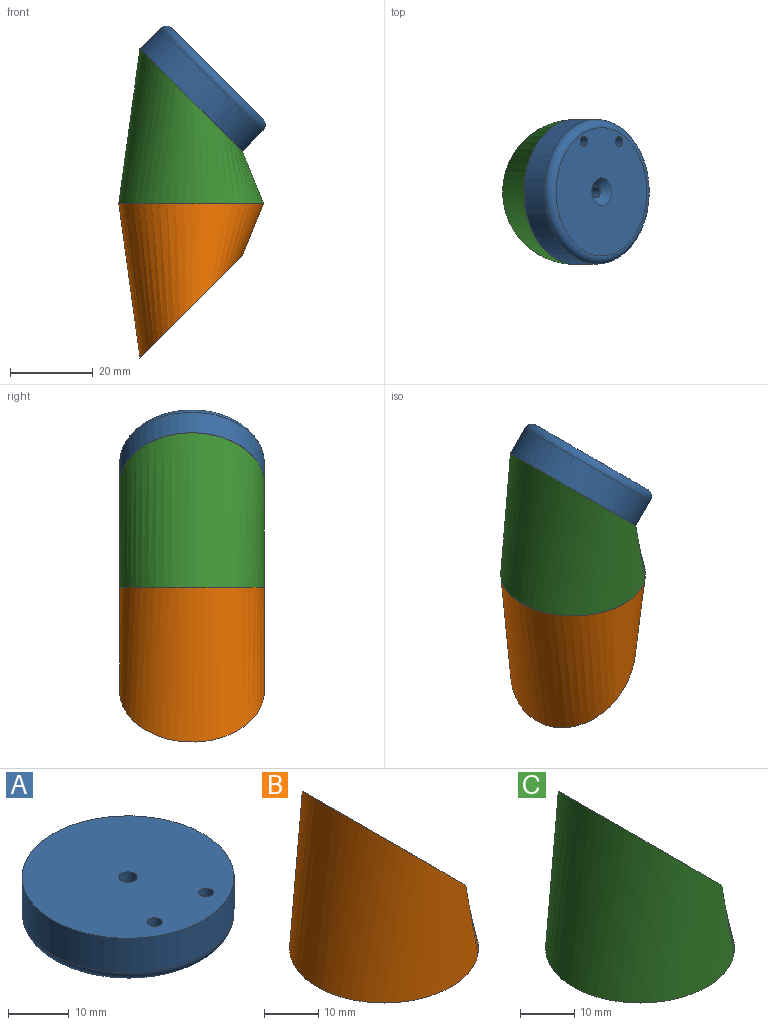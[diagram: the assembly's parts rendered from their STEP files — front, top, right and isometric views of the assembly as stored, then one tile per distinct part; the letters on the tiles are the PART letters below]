
ASSEMBLY  parts=3 mates=2
PART A: 8 faces, bbox 37.9x37.9x9 mm
  f0: cylinder r=17.5mm len=35mm, axis (0,0,-1), area 769.7mm2, adj f1,f7
  f1: plane 35x35mm, normal (0,0,1), area 945.2mm2, adj f0,f3,f5,f6
  f2: plane 31x31mm, normal (0,0,-1), area 709.5mm2, adj f4,f5,f6,f7
  f3: cylinder r=1.5mm len=7.14mm, axis (0,0,-1), area 67.3mm2, adj f1,f4
  f4: cone r=1.5mm half-angle=45deg, axis (0,0,-1), area 40.2mm2, adj f2,f3
  f5: cylinder r=1.25mm len=9mm, axis (0,0,-1), area 70.7mm2, adj f1,f2
  f6: cylinder r=1.25mm len=9mm, axis (0,0,-1), area 70.7mm2, adj f1,f2
  f7: torus R=15.5mm, axis (0,0,1), area 331.1mm2, adj f0,f2
PART B: 9 faces, bbox 35x35x37.4 mm
  f0: plane 35x35mm, normal (0,0,-1), area 956.3mm2, adj f2,f3
  f1: plane 35x24.75mm, normal (0.71,0,0.71), area 582mm2, adj f2,f5
  f2: bspline ~37.37x35mm, area 2581.6mm2, adj f0,f1
  f3: cylinder r=1.35mm len=12mm, axis (0,0,-1), area 101.8mm2, adj f0,f4
  f4: plane 2.7x2.7mm, normal (0,0,-1), area 5.7mm2, adj f3
  f5: cylinder r=11mm len=22mm, axis (0.71,0,0.71), area 449.2mm2, adj f1,f6
  f6: plane 22x15.56mm, normal (0.71,0,0.71), area 375.2mm2, adj f5,f7
  f7: cylinder r=1.25mm len=7.78mm, axis (0.71,0,0.71), area 66.8mm2, adj f6,f8
  f8: plane 2.5x1.77mm, normal (0.71,0,0.71), area 4.9mm2, adj f7
PART C: 8 faces, bbox 35x35x37.4 mm
  f0: cylinder r=1.35mm len=10mm, axis (0,0,-1), area 84.8mm2, adj f1,f5
  f1: plane 35x35mm, normal (0,0,-1), area 956.3mm2, adj f0,f3
  f2: plane 35x24.75mm, normal (0.71,0,0.71), area 851.1mm2, adj f3,f4
  f3: bspline ~37.37x35mm, area 2581.6mm2, adj f1,f2
  f4: cylinder r=5mm len=20.07mm, axis (0,0,-1), area 464.2mm2, adj f2,f5,f6
  f5: plane 10x10mm, normal (0,0,1), area 72.8mm2, adj f0,f4
  f6: cylinder r=1.25mm len=10.38mm, axis (0.71,0,0.71), area 86.7mm2, adj f4,f7
  f7: plane 2.5x1.77mm, normal (0.71,0,0.71), area 4.9mm2, adj f6
PLACE A rot(axis=(0.92,0,-0.38),180deg) t=(31.19,-46.88,37.89)mm
PLACE B rot(axis=(1,0,0),180deg) t=(24.82,-46.88,-18.48)mm
PLACE C t=(24.82,-46.88,31.52)mm
MATE revolute C.f6 <-> A.f0  axis (0.71,0,0.71) through (24.82,-46.88,31.52)mm
MATE revolute B.f3 <-> C.f0  axis (0,0,1) through (24.82,-46.88,6.52)mm
